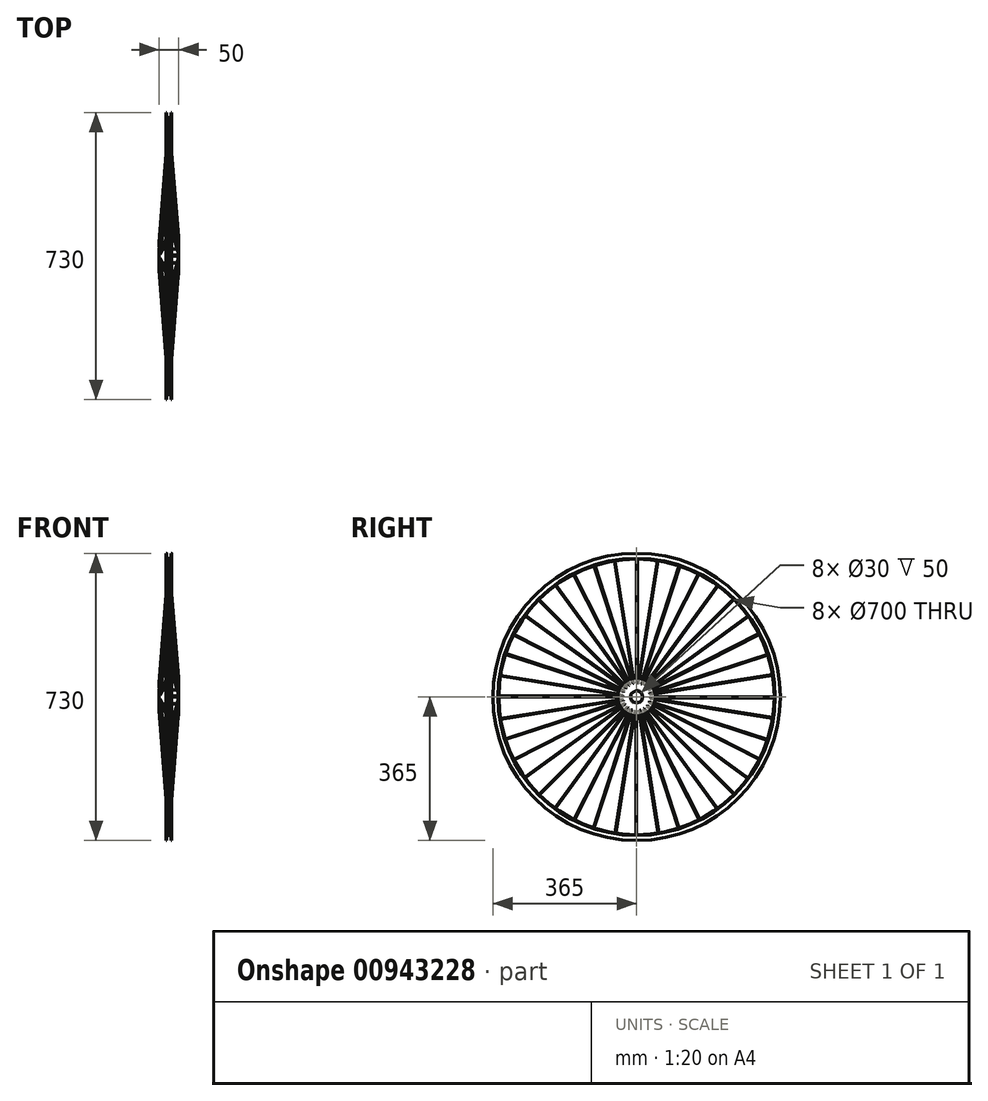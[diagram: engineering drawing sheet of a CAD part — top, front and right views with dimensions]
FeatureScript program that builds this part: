
annotation { "Feature Type Name" : "Feature", "Feature Type Description" : "" }
export const myFeature = defineFeature(function(context is Context, id is Id, definition is map)
    precondition{}
    {
        {
            var Q0;
            Q0=qCreatedBy(makeId("Front.planeOp"),FACE);
            var sketch = newSketch(context, id + "F0", { "sketchPlane" : qUnion([Q0])});
            skLineSegment(sketch, "E0", {"start": v(0, 352) * mm, "end": v(5, 352) * mm});
            skLineSegment(sketch, "E1", {"start": v(5, 352) * mm, "end": v(7.36, 353.85) * mm});
            skLineSegment(sketch, "E2", {"start": v(7.36, 353.85) * mm, "end": v(7.36, 363.85) * mm});
            skLineSegment(sketch, "E3", {"start": v(0, 352) * mm, "end": v(-5, 352) * mm});
            skLineSegment(sketch, "E4", {"start": v(-5, 352) * mm, "end": v(-6.85, 354.36) * mm});
            skLineSegment(sketch, "E5", {"start": v(-6.85, 354.36) * mm, "end": v(-6.85, 364.36) * mm});
            skLineSegment(sketch, "E6", {"start": v(0, 352) * mm, "end": v(0, 0) * mm});
            skLineSegment(sketch, "E7", {"start": v(0, 0) * mm, "end": v(0, 20) * mm});
            skLineSegment(sketch, "E8", {"start": v(0, 20) * mm, "end": v(25, 20) * mm});
            skLineSegment(sketch, "E9", {"start": v(25, 20) * mm, "end": v(25, 0) * mm});
            skLineSegment(sketch, "E10", {"start": v(0, 20) * mm, "end": v(-25, 20) * mm});
            skLineSegment(sketch, "E11", {"start": v(-25, 20) * mm, "end": v(-25, 0) * mm});
            skLineSegment(sketch, "E12", {"start": v(25, 20) * mm, "end": v(25, 50) * mm});
            skLineSegment(sketch, "E13", {"start": v(-25, 20) * mm, "end": v(-25, 50) * mm});
            skLineSegment(sketch, "E14", {"start": v(-74.65, 0) * mm, "end": v(75.16, 0) * mm});
            skLineSegment(sketch, "E15", {"start": v(-25, 35) * mm, "end": v(0, 352) * mm});
            skLineSegment(sketch, "E16", {"start": v(25, 35) * mm, "end": v(0, 352) * mm});
            skSolve(sketch);
        }
        {
            var Q0;
            Q0=qCreatedBy(makeId("Front.planeOp"),FACE);
            var sketch = newSketch(context, id + "F1", { "sketchPlane" : qUnion([Q0])});
            skLineSegment(sketch, "E17", {"start": v(0, 0) * mm, "end": v(0, 350) * mm});
            skLineSegment(sketch, "E18.bottom", {"start": v(-7, 350) * mm, "end": v(7, 350) * mm});
            skLineSegment(sketch, "E18.top", {"start": v(-7, 365) * mm, "end": v(7, 365) * mm});
            skLineSegment(sketch, "E18.left", {"start": v(-7, 350) * mm, "end": v(-7, 365) * mm});
            skLineSegment(sketch, "E18.right", {"start": v(7, 350) * mm, "end": v(7, 365) * mm});
            skLineSegment(sketch, "E19", {"start": v(-7, 352) * mm, "end": v(-5, 350) * mm});
            skLineSegment(sketch, "E20", {"start": v(5, 350) * mm, "end": v(7, 352) * mm});
            skLineSegment(sketch, "E21.0", {"start": v(-6, 351) * mm, "end": v(-6, 365) * mm});
            skLineSegment(sketch, "E21.1", {"start": v(-6, 351) * mm, "end": v(6, 351) * mm});
            skLineSegment(sketch, "E21.2", {"start": v(6, 351) * mm, "end": v(6, 365) * mm});
            skLineSegment(sketch, "E22.0", {"start": v(-6.3, 352.7) * mm, "end": v(-4.3, 350.7) * mm});
            skLineSegment(sketch, "E23.0", {"start": v(4.3, 350.7) * mm, "end": v(6.3, 352.7) * mm});
            skLineSegment(sketch, "E24.bottom", {"start": v(0, 0) * mm, "end": v(-25, 0) * mm});
            skLineSegment(sketch, "E24.top", {"start": v(0, 18) * mm, "end": v(-25, 18) * mm});
            skLineSegment(sketch, "E24.left", {"start": v(0, 0) * mm, "end": v(0, 18) * mm});
            skLineSegment(sketch, "E24.right", {"start": v(-25, 0) * mm, "end": v(-25, 18) * mm});
            skLineSegment(sketch, "E25.bottom", {"start": v(-25, 18) * mm, "end": v(-23, 18) * mm});
            skLineSegment(sketch, "E25.top", {"start": v(-25, 48) * mm, "end": v(-23, 48) * mm});
            skLineSegment(sketch, "E25.left", {"start": v(-25, 18) * mm, "end": v(-25, 48) * mm});
            skLineSegment(sketch, "E25.right", {"start": v(-23, 18) * mm, "end": v(-23, 48) * mm});
            skLineSegment(sketch, "E26.MirrorCS", {"start": v(25, 48) * mm, "end": v(23, 48) * mm});
            skLineSegment(sketch, "E27.MirrorCS", {"start": v(25, 18) * mm, "end": v(25, 48) * mm});
            skLineSegment(sketch, "E28.MirrorCS", {"start": v(23, 18) * mm, "end": v(23, 48) * mm});
            skLineSegment(sketch, "E29.MirrorCS", {"start": v(0, 18) * mm, "end": v(25, 18) * mm});
            skLineSegment(sketch, "E30.MirrorCS", {"start": v(0, 0) * mm, "end": v(25, 0) * mm});
            skLineSegment(sketch, "E31.MirrorCS", {"start": v(25, 0) * mm, "end": v(25, 18) * mm});
            skLineSegment(sketch, "E32", {"start": v(-25, 15) * mm, "end": v(25, 15) * mm});
            skSolve(sketch);
        }
        {
            var Q0;
            Q0=makeQuery(id+"F1.imprint","IMPRINT",FACE,{"disambiguationData":[TD([[makeQuery(id+"F1.imprint","IMPRINT",EDGE,{"derivedFrom":sQuery(id+"F1.wireOp",EDGE,"E26.MirrorCS")}),1.0]])]});
            var Q1;
            {var subQ0=sQuery(id+"F1.wireOp",EDGE,"E31.MirrorCS");var subQ3=sQuery(id+"F1.wireOp",EDGE,"E32");var subQ4=makeQuery(id+"F1.imprint","INTERSECT",VERTEX,{"derivedFrom":[subQ0,subQ3]});Q1=makeQuery(id+"F1.imprint","IMPRINT",FACE,{"disambiguationData":[TD([[makeQuery(id+"F1.imprint","IMPRINT",EDGE,{"disambiguationData":[TD([[subQ4,1.0]])],"derivedFrom":subQ3}),1.0]])]});}
            var Q2;
            {var subQ5=sQuery(id+"F1.wireOp",EDGE,"E24.top");Q2=makeQuery(id+"F1.imprint","IMPRINT",FACE,{"disambiguationData":[TD([[makeQuery(id+"F1.imprint","IMPRINT",EDGE,{"derivedFrom":subQ5}),1.0]])]});}
            var Q3;
            Q3=makeQuery(id+"F1.imprint","IMPRINT",FACE,{"disambiguationData":[TD([[makeQuery(id+"F1.imprint","IMPRINT",EDGE,{"derivedFrom":sQuery(id+"F1.wireOp",EDGE,"E25.bottom")}),1.0]])]});
            var Q4;
            {var subQ1=sQuery(id+"F1.wireOp",EDGE,"E18.right");var subQ6=sQuery(id+"F1.wireOp",EDGE,"E18.top");var subQ7=makeQuery(id+"F1.imprint","INTERSECT",VERTEX,{"derivedFrom":[subQ6,subQ1]});Q4=makeQuery(id+"F1.imprint","IMPRINT",FACE,{"disambiguationData":[TD([[makeQuery(id+"F1.imprint","IMPRINT",EDGE,{"disambiguationData":[TD([[subQ7,1.0]])],"derivedFrom":subQ6}),-1.0]])]});}
            var Q5;
            {var subQ1=sQuery(id+"F1.wireOp",EDGE,"E21.1");var subQ3=sQuery(id+"F1.wireOp",EDGE,"E23.0");var subQ4=makeQuery(id+"F1.imprint","INTERSECT",VERTEX,{"derivedFrom":[subQ1,subQ3]});Q5=makeQuery(id+"F1.imprint","IMPRINT",FACE,{"disambiguationData":[TD([[makeQuery(id+"F1.imprint","IMPRINT",EDGE,{"disambiguationData":[TD([[subQ4,-1.0]])],"derivedFrom":subQ3}),-1.0]])]});}
            var Q6;
            {var subQ1=sQuery(id+"F1.wireOp",EDGE,"E18.bottom");var subQ5=makeQuery(id+"F1.imprint","IMPRINT",VERTEX,{"derivedFrom":subQ1});Q6=makeQuery(id+"F1.imprint","IMPRINT",FACE,{"disambiguationData":[TD([[makeQuery(id+"F1.imprint","IMPRINT",EDGE,{"disambiguationData":[TD([[subQ5,1.0]])],"derivedFrom":subQ1}),1.0]])]});}
            var Q7;
            {var subQ1=sQuery(id+"F1.wireOp",EDGE,"E21.0");var subQ3=sQuery(id+"F1.wireOp",EDGE,"E22.0");var subQ4=makeQuery(id+"F1.imprint","INTERSECT",VERTEX,{"derivedFrom":[subQ1,subQ3]});Q7=makeQuery(id+"F1.imprint","IMPRINT",FACE,{"disambiguationData":[TD([[makeQuery(id+"F1.imprint","IMPRINT",EDGE,{"disambiguationData":[TD([[subQ4,-1.0]])],"derivedFrom":subQ3}),-1.0]])]});}
            var Q8;
            {var subQ4=sQuery(id+"F1.wireOp",EDGE,"E18.left");var subQ5=sQuery(id+"F1.wireOp",EDGE,"E18.top");var subQ6=makeQuery(id+"F1.imprint","INTERSECT",VERTEX,{"derivedFrom":[subQ5,subQ4]});Q8=makeQuery(id+"F1.imprint","IMPRINT",FACE,{"disambiguationData":[TD([[makeQuery(id+"F1.imprint","IMPRINT",EDGE,{"disambiguationData":[TD([[subQ6,-1.0]])],"derivedFrom":subQ5}),-1.0]])]});}
            var Q9;
            {var subQ5=sQuery(id+"F1.wireOp",EDGE,"yEOQuf01-vHYe-JAYC-lFGH-x6cpkkwGujmB");Q9=makeQuery(id+"F1.imprint","IMPRINT",FACE,{"disambiguationData":[TD([[makeQuery(id+"F1.imprint","IMPRINT",EDGE,{"derivedFrom":subQ5}),1.0]])]});}
            var Q10;
            {var subQ1=sQuery(id+"F1.wireOp",EDGE,"DnqzMhMG-7us7-yUhr-n8Ny-UNY0jh0rZNmx");Q10=makeQuery(id+"F1.imprint","IMPRINT",FACE,{"disambiguationData":[TD([[makeQuery(id+"F1.imprint","IMPRINT",EDGE,{"derivedFrom":subQ1}),1.0]])]});}
            var Q11;
            {var subQ2=sQuery(id+"F1.wireOp",EDGE,"b3702c39-863d-4951-96f5-6276b23e51460.MirrorCS");Q11=makeQuery(id+"F1.imprint","IMPRINT",FACE,{"disambiguationData":[TD([[makeQuery(id+"F1.imprint","IMPRINT",EDGE,{"derivedFrom":subQ2}),-1.0]])]});}
            var Q12;
            Q12=sQuery(id+"F0.wireOp",EDGE,"E2");
            var Q13;
            Q13=sQuery(id+"F0.wireOp",EDGE,"E0");
            var Q14;
            Q14=sQuery(id+"F0.wireOp",EDGE,"E3");
            var Q15;
            Q15=sQuery(id+"F0.wireOp",EDGE,"E5");
            var Q16;
            Q16=sQuery(id+"F0.wireOp",EDGE,"E4");
            var Q17;
            Q17=sQuery(id+"F0.wireOp",EDGE,"E1");
            var Q18;
            Q18=sQuery(id+"F0.wireOp",EDGE,"E13");
            var Q19;
            Q19=sQuery(id+"F0.wireOp",EDGE,"E10");
            var Q20;
            Q20=sQuery(id+"F0.wireOp",EDGE,"E8");
            var Q21;
            Q21=sQuery(id+"F0.wireOp",EDGE,"E12");
            var Q22;
            Q22=sQuery(id+"F1.wireOp",EDGE,"E30.MirrorCS");
            revolve(context, id + "F2", {"surfaceOperationType" : NewSurfaceOperationType.NEW, "entities" : qUnion([Q0, Q1, Q2, Q3, Q4, Q5, Q6, Q7, Q8, Q9, Q10, Q11]), "surfaceEntities" : qUnion([Q12, Q13, Q14, Q15, Q16, Q17, Q18, Q19, Q20, Q21]), "axis" : qUnion([Q22]), "revolveType" : RevolveType.FULL});
        }
        {
            var Q0;
            Q0=sQuery(id+"F0.wireOp",EDGE,"E15");
            extrude(context, id + "F3", {"bodyType" : ToolBodyType.SURFACE, "surfaceEntities" : qUnion([Q0]), "depth" : 2 * mm, "offsetDistance" : 25 * mm});
        }
        {
            var Q0;
            Q0=makeQuery(id+"F3.opExtrude","SWEPT_FACE",FACE,{"disambiguationData":[OSD([sQuery(id+"F0.wireOp",EDGE,"E15")])]});
            extrude(context, id + "F4", {"entities" : qUnion([Q0]), "depth" : 2 * mm, "offsetDistance" : 25 * mm});
        }
        {
            var Q0;
            Q0=qCreatedBy(makeId("Right.planeOp"),FACE);
            var sketch = newSketch(context, id + "F5", { "sketchPlane" : qUnion([Q0])});
            skLineSegment(sketch, "E33", {"start": v(73.54, 0) * mm, "end": v(-220.1, 0) * mm});
            skLineSegment(sketch, "E34", {"start": v(-220.1, 0) * mm, "end": v(168.97, 0) * mm});
            skSolve(sketch);
        }
        {
            var Q0;
            Q0=makeQuery(id+"F4.opExtrude","SWEPT_BODY",BODY,{"disambiguationData":[OSD([sQuery(id+"F0.wireOp",EDGE,"E15")])]});
            var Q1;
            Q1=sQuery(id+"F0.wireOp",EDGE,"E14");
            circularPattern(context, id + "F6", {"entities" : qUnion([Q0]), "axis" : qUnion([Q1]), "angle" : 360 * degree, "instanceCount" : 20, "equalSpace" : true});
        }
        {
            var Q0;
            Q0=makeQuery(id+"F6.opPattern","COPY",BODY,{"derivedFrom":makeQuery(id+"F4.opExtrude","SWEPT_BODY",BODY,{"disambiguationData":[OSD([sQuery(id+"F0.wireOp",EDGE,"E15")])]}),"instanceName":"9"});
            var Q1;
            Q1=makeQuery(id+"F6.opPattern","COPY",BODY,{"derivedFrom":makeQuery(id+"F4.opExtrude","SWEPT_BODY",BODY,{"disambiguationData":[OSD([sQuery(id+"F0.wireOp",EDGE,"E15")])]}),"instanceName":"8"});
            var Q2;
            Q2=makeQuery(id+"F6.opPattern","COPY",BODY,{"derivedFrom":makeQuery(id+"F4.opExtrude","SWEPT_BODY",BODY,{"disambiguationData":[OSD([sQuery(id+"F0.wireOp",EDGE,"E15")])]}),"instanceName":"7"});
            var Q3;
            Q3=makeQuery(id+"F6.opPattern","COPY",BODY,{"derivedFrom":makeQuery(id+"F4.opExtrude","SWEPT_BODY",BODY,{"disambiguationData":[OSD([sQuery(id+"F0.wireOp",EDGE,"E15")])]}),"instanceName":"6"});
            var Q4;
            Q4=makeQuery(id+"F6.opPattern","COPY",BODY,{"derivedFrom":makeQuery(id+"F4.opExtrude","SWEPT_BODY",BODY,{"disambiguationData":[OSD([sQuery(id+"F0.wireOp",EDGE,"E15")])]}),"instanceName":"5"});
            var Q5;
            Q5=makeQuery(id+"F6.opPattern","COPY",BODY,{"derivedFrom":makeQuery(id+"F4.opExtrude","SWEPT_BODY",BODY,{"disambiguationData":[OSD([sQuery(id+"F0.wireOp",EDGE,"E15")])]}),"instanceName":"4"});
            var Q6;
            Q6=makeQuery(id+"F6.opPattern","COPY",BODY,{"derivedFrom":makeQuery(id+"F4.opExtrude","SWEPT_BODY",BODY,{"disambiguationData":[OSD([sQuery(id+"F0.wireOp",EDGE,"E15")])]}),"instanceName":"2"});
            var Q7;
            Q7=makeQuery(id+"F6.opPattern","COPY",BODY,{"derivedFrom":makeQuery(id+"F4.opExtrude","SWEPT_BODY",BODY,{"disambiguationData":[OSD([sQuery(id+"F0.wireOp",EDGE,"E15")])]}),"instanceName":"3"});
            var Q8;
            Q8=makeQuery(id+"F6.opPattern","COPY",BODY,{"derivedFrom":makeQuery(id+"F4.opExtrude","SWEPT_BODY",BODY,{"disambiguationData":[OSD([sQuery(id+"F0.wireOp",EDGE,"E15")])]}),"instanceName":"1"});
            var Q9;
            Q9=makeQuery(id+"F4.opExtrude","SWEPT_BODY",BODY,{"disambiguationData":[OSD([sQuery(id+"F0.wireOp",EDGE,"E15")])]});
            var Q10;
            Q10=makeQuery(id+"F6.opPattern","COPY",BODY,{"derivedFrom":makeQuery(id+"F4.opExtrude","SWEPT_BODY",BODY,{"disambiguationData":[OSD([sQuery(id+"F0.wireOp",EDGE,"E15")])]}),"instanceName":"19"});
            var Q11;
            Q11=makeQuery(id+"F6.opPattern","COPY",BODY,{"derivedFrom":makeQuery(id+"F4.opExtrude","SWEPT_BODY",BODY,{"disambiguationData":[OSD([sQuery(id+"F0.wireOp",EDGE,"E15")])]}),"instanceName":"18"});
            var Q12;
            Q12=makeQuery(id+"F6.opPattern","COPY",BODY,{"derivedFrom":makeQuery(id+"F4.opExtrude","SWEPT_BODY",BODY,{"disambiguationData":[OSD([sQuery(id+"F0.wireOp",EDGE,"E15")])]}),"instanceName":"17"});
            var Q13;
            Q13=makeQuery(id+"F6.opPattern","COPY",BODY,{"derivedFrom":makeQuery(id+"F4.opExtrude","SWEPT_BODY",BODY,{"disambiguationData":[OSD([sQuery(id+"F0.wireOp",EDGE,"E15")])]}),"instanceName":"16"});
            var Q14;
            Q14=makeQuery(id+"F6.opPattern","COPY",BODY,{"derivedFrom":makeQuery(id+"F4.opExtrude","SWEPT_BODY",BODY,{"disambiguationData":[OSD([sQuery(id+"F0.wireOp",EDGE,"E15")])]}),"instanceName":"15"});
            var Q15;
            Q15=makeQuery(id+"F6.opPattern","COPY",BODY,{"derivedFrom":makeQuery(id+"F4.opExtrude","SWEPT_BODY",BODY,{"disambiguationData":[OSD([sQuery(id+"F0.wireOp",EDGE,"E15")])]}),"instanceName":"14"});
            var Q16;
            Q16=makeQuery(id+"F6.opPattern","COPY",BODY,{"derivedFrom":makeQuery(id+"F4.opExtrude","SWEPT_BODY",BODY,{"disambiguationData":[OSD([sQuery(id+"F0.wireOp",EDGE,"E15")])]}),"instanceName":"12"});
            var Q17;
            Q17=makeQuery(id+"F6.opPattern","COPY",BODY,{"derivedFrom":makeQuery(id+"F4.opExtrude","SWEPT_BODY",BODY,{"disambiguationData":[OSD([sQuery(id+"F0.wireOp",EDGE,"E15")])]}),"instanceName":"13"});
            var Q18;
            Q18=makeQuery(id+"F6.opPattern","COPY",BODY,{"derivedFrom":makeQuery(id+"F4.opExtrude","SWEPT_BODY",BODY,{"disambiguationData":[OSD([sQuery(id+"F0.wireOp",EDGE,"E15")])]}),"instanceName":"11"});
            var Q19;
            Q19=makeQuery(id+"F6.opPattern","COPY",BODY,{"derivedFrom":makeQuery(id+"F4.opExtrude","SWEPT_BODY",BODY,{"disambiguationData":[OSD([sQuery(id+"F0.wireOp",EDGE,"E15")])]}),"instanceName":"10"});
            var Q20;
            Q20=sQuery(id+"F5.wireOp",EDGE,"E34");
            transform(context, id + "F7", {"entities" : qUnion([Q0, Q1, Q2, Q3, Q4, Q5, Q6, Q7, Q8, Q9, Q10, Q11, Q12, Q13, Q14, Q15, Q16, Q17, Q18, Q19]), "transformType" : TransformType.ROTATION, "transformAxis" : qUnion([Q20]), "angle" : 180 * degree, "makeCopy" : true});
        }
        {
            var Q0;
            Q0=makeQuery(id+"F4.opExtrude","SWEPT_BODY",BODY,{"disambiguationData":[OSD([sQuery(id+"F0.wireOp",EDGE,"E15")])]});
            var Q1;
            Q1=makeQuery(id+"F6.opPattern","COPY",BODY,{"derivedFrom":makeQuery(id+"F4.opExtrude","SWEPT_BODY",BODY,{"disambiguationData":[OSD([sQuery(id+"F0.wireOp",EDGE,"E15")])]}),"instanceName":"1"});
            var Q2;
            Q2=makeQuery(id+"F6.opPattern","COPY",BODY,{"derivedFrom":makeQuery(id+"F4.opExtrude","SWEPT_BODY",BODY,{"disambiguationData":[OSD([sQuery(id+"F0.wireOp",EDGE,"E15")])]}),"instanceName":"2"});
            var Q3;
            Q3=makeQuery(id+"F6.opPattern","COPY",BODY,{"derivedFrom":makeQuery(id+"F4.opExtrude","SWEPT_BODY",BODY,{"disambiguationData":[OSD([sQuery(id+"F0.wireOp",EDGE,"E15")])]}),"instanceName":"3"});
            var Q4;
            Q4=makeQuery(id+"F6.opPattern","COPY",BODY,{"derivedFrom":makeQuery(id+"F4.opExtrude","SWEPT_BODY",BODY,{"disambiguationData":[OSD([sQuery(id+"F0.wireOp",EDGE,"E15")])]}),"instanceName":"4"});
            var Q5;
            Q5=makeQuery(id+"F6.opPattern","COPY",BODY,{"derivedFrom":makeQuery(id+"F4.opExtrude","SWEPT_BODY",BODY,{"disambiguationData":[OSD([sQuery(id+"F0.wireOp",EDGE,"E15")])]}),"instanceName":"5"});
            var Q6;
            Q6=makeQuery(id+"F6.opPattern","COPY",BODY,{"derivedFrom":makeQuery(id+"F4.opExtrude","SWEPT_BODY",BODY,{"disambiguationData":[OSD([sQuery(id+"F0.wireOp",EDGE,"E15")])]}),"instanceName":"6"});
            var Q7;
            Q7=makeQuery(id+"F6.opPattern","COPY",BODY,{"derivedFrom":makeQuery(id+"F4.opExtrude","SWEPT_BODY",BODY,{"disambiguationData":[OSD([sQuery(id+"F0.wireOp",EDGE,"E15")])]}),"instanceName":"7"});
            var Q8;
            Q8=makeQuery(id+"F6.opPattern","COPY",BODY,{"derivedFrom":makeQuery(id+"F4.opExtrude","SWEPT_BODY",BODY,{"disambiguationData":[OSD([sQuery(id+"F0.wireOp",EDGE,"E15")])]}),"instanceName":"8"});
            var Q9;
            Q9=makeQuery(id+"F6.opPattern","COPY",BODY,{"derivedFrom":makeQuery(id+"F4.opExtrude","SWEPT_BODY",BODY,{"disambiguationData":[OSD([sQuery(id+"F0.wireOp",EDGE,"E15")])]}),"instanceName":"9"});
            var Q10;
            Q10=makeQuery(id+"F6.opPattern","COPY",BODY,{"derivedFrom":makeQuery(id+"F4.opExtrude","SWEPT_BODY",BODY,{"disambiguationData":[OSD([sQuery(id+"F0.wireOp",EDGE,"E15")])]}),"instanceName":"10"});
            var Q11;
            Q11=makeQuery(id+"F6.opPattern","COPY",BODY,{"derivedFrom":makeQuery(id+"F4.opExtrude","SWEPT_BODY",BODY,{"disambiguationData":[OSD([sQuery(id+"F0.wireOp",EDGE,"E15")])]}),"instanceName":"11"});
            var Q12;
            Q12=makeQuery(id+"F6.opPattern","COPY",BODY,{"derivedFrom":makeQuery(id+"F4.opExtrude","SWEPT_BODY",BODY,{"disambiguationData":[OSD([sQuery(id+"F0.wireOp",EDGE,"E15")])]}),"instanceName":"12"});
            var Q13;
            Q13=makeQuery(id+"F6.opPattern","COPY",BODY,{"derivedFrom":makeQuery(id+"F4.opExtrude","SWEPT_BODY",BODY,{"disambiguationData":[OSD([sQuery(id+"F0.wireOp",EDGE,"E15")])]}),"instanceName":"13"});
            var Q14;
            Q14=makeQuery(id+"F6.opPattern","COPY",BODY,{"derivedFrom":makeQuery(id+"F4.opExtrude","SWEPT_BODY",BODY,{"disambiguationData":[OSD([sQuery(id+"F0.wireOp",EDGE,"E15")])]}),"instanceName":"14"});
            var Q15;
            Q15=makeQuery(id+"F6.opPattern","COPY",BODY,{"derivedFrom":makeQuery(id+"F4.opExtrude","SWEPT_BODY",BODY,{"disambiguationData":[OSD([sQuery(id+"F0.wireOp",EDGE,"E15")])]}),"instanceName":"15"});
            var Q16;
            Q16=makeQuery(id+"F6.opPattern","COPY",BODY,{"derivedFrom":makeQuery(id+"F4.opExtrude","SWEPT_BODY",BODY,{"disambiguationData":[OSD([sQuery(id+"F0.wireOp",EDGE,"E15")])]}),"instanceName":"16"});
            var Q17;
            Q17=makeQuery(id+"F6.opPattern","COPY",BODY,{"derivedFrom":makeQuery(id+"F4.opExtrude","SWEPT_BODY",BODY,{"disambiguationData":[OSD([sQuery(id+"F0.wireOp",EDGE,"E15")])]}),"instanceName":"17"});
            var Q18;
            Q18=makeQuery(id+"F6.opPattern","COPY",BODY,{"derivedFrom":makeQuery(id+"F4.opExtrude","SWEPT_BODY",BODY,{"disambiguationData":[OSD([sQuery(id+"F0.wireOp",EDGE,"E15")])]}),"instanceName":"18"});
            var Q19;
            Q19=makeQuery(id+"F6.opPattern","COPY",BODY,{"derivedFrom":makeQuery(id+"F4.opExtrude","SWEPT_BODY",BODY,{"disambiguationData":[OSD([sQuery(id+"F0.wireOp",EDGE,"E15")])]}),"instanceName":"19"});
            var Q20;
            Q20=sQuery(id+"F0.wireOp",EDGE,"E14");
            var Q21;
            Q21=sQuery(id+"F0.wireOp",EDGE,"E14");
            transform(context, id + "F8", {"entities" : qUnion([Q0, Q1, Q2, Q3, Q4, Q5, Q6, Q7, Q8, Q9, Q10, Q11, Q12, Q13, Q14, Q15, Q16, Q17, Q18, Q19]), "transformType" : TransformType.ROTATION, "transformAxis" : qUnion([Q21]), "angle" : 9 * degree, "makeCopy" : false});
        }
    });
